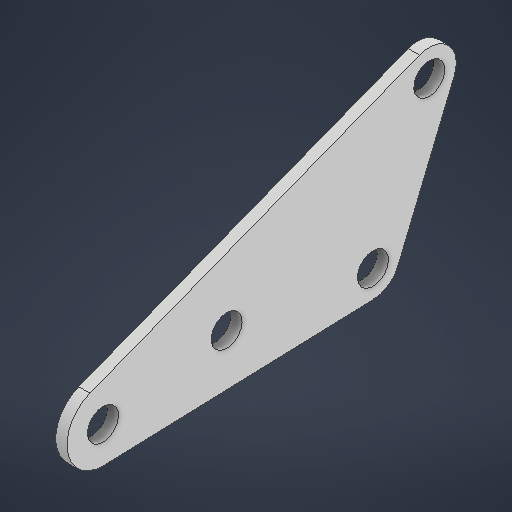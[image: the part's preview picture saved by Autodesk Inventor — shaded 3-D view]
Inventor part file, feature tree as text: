
AUTODESK INVENTOR PART (.ipt)
format: ipt  version: 2025.2 (Build 292293000, 293)  size: 200,704 bytes
history: native  units: in
note: dims shown in document units (in); Inventor stores cm internally (conversion verified against a paired STEP export)
features: extrude x1, sketch x1
ambient origin geometry x8: Origin, YZ Plane, XZ Plane, XY Plane, X Axis, Y Axis, Z Axis, Center Point
bodies: Solid1 (feature_tree)
feature tree (2):
  extrude  "Extrusion1"  Depth=0.0625in
  sketch  "Sketch1"  dims[d0=0.172in d1=0.3in d3=0.172in d4=0.4in d8=0.172in d11=0.172in d12=0.3in d13=0.3in d20=0.0625in d21=0.0in]
